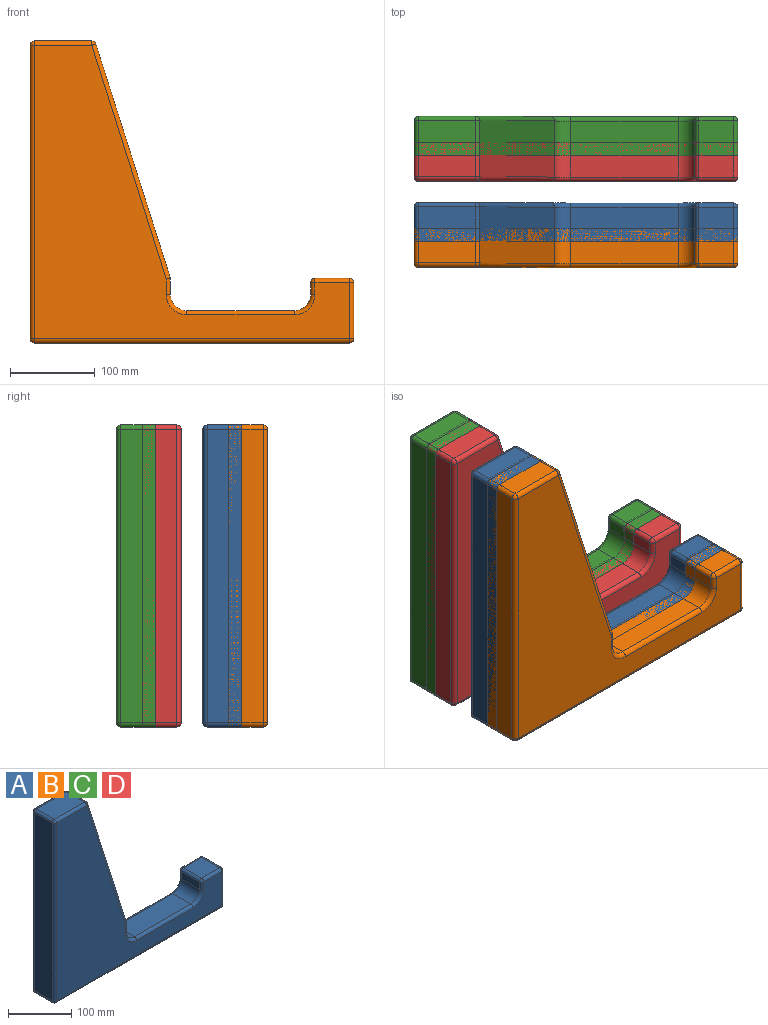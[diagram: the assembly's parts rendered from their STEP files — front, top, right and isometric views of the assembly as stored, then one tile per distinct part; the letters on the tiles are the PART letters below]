
ASSEMBLY  parts=4 mates=1
PART A: 56 faces, bbox 381x50.8x355.6 mm
  f0: plane 345.44x40.64mm, normal (-1,0,0), area 14038.7mm2, adj f23,f32,f33,f34
  f1: plane 370.84x40.64mm, normal (0,0,-1), area 15070.9mm2, adj f14,f22,f23,f24
  f2: plane 66.04x40.64mm, normal (1,0,0), area 2683.9mm2, adj f13,f14,f15,f16
  f3: plane 40.64x40.64mm, normal (0,0,1), area 1651.6mm2, adj f16,f21,f25,f26
  f4: plane 40.64x13.97mm, normal (-1,0,0), area 567.7mm2, adj f5,f26,f31,f35
  f5: cylinder r=19.05mm len=40.64mm, axis (0,1,0), area 1216.1mm2, adj f4,f6,f36,f39
  f6: plane 127x40.64mm, normal (0,0,1), area 5161.3mm2, adj f5,f7,f40,f44
  f7: cylinder r=19.05mm len=40.64mm, axis (0,1,0), area 1216.1mm2, adj f6,f8,f45,f48
  f8: plane 40.64x18.26mm, normal (1,0,0), area 742.1mm2, adj f7,f49,f52,f55
  f9: plane 275.11x87.53mm, normal (0.95,0,0.3), area 11732.7mm2, adj f42,f50,f51,f55
  f10: plane 67.41x40.64mm, normal (0,0,1), area 2739.4mm2, adj f33,f41,f42,f43
  f11: plane 370.84x345.44mm, normal (0,-1,0), area 49312.2mm2, adj f13,f21,f22,f31,f32,f36,f40,f41
  f12: plane 370.84x345.44mm, normal (0,1,0), area 49312.2mm2, adj f15,f24,f25,f34,f35,f39,f43,f44
  f13: cylinder r=5.08mm len=66.04mm, axis (0,0,-1), area 527mm2, adj f2,f11,f17,f18
  f14: cylinder r=5.08mm len=40.64mm, axis (0,1,0), area 324.3mm2, adj f1,f2,f18,f19
  f15: cylinder r=5.08mm len=66.04mm, axis (0,0,1), area 527mm2, adj f2,f12,f19,f20
  f16: cylinder r=5.08mm len=40.64mm, axis (0,-1,0), area 324.3mm2, adj f2,f3,f17,f20
  f17: sphere r=5.08mm, area 40.5mm2, adj f13,f16,f21
  f18: sphere r=5.08mm, area 40.5mm2, adj f13,f14,f22
  f19: sphere r=5.08mm, area 40.5mm2, adj f14,f15,f24
  f20: sphere r=5.08mm, area 40.5mm2, adj f15,f16,f25
  f21: cylinder r=5.08mm len=40.64mm, axis (1,0,0), area 324.3mm2, adj f3,f11,f17,f27
  f22: cylinder r=5.08mm len=370.84mm, axis (-1,0,0), area 2959.2mm2, adj f1,f11,f18,f28
  f23: cylinder r=5.08mm len=40.64mm, axis (0,-1,0), area 324.3mm2, adj f0,f1,f28,f29
  f24: cylinder r=5.08mm len=370.84mm, axis (1,0,0), area 2959.2mm2, adj f1,f12,f19,f29
  f25: cylinder r=5.08mm len=40.64mm, axis (-1,0,0), area 324.3mm2, adj f3,f12,f20,f30
  f26: cylinder r=5.08mm len=40.64mm, axis (0,-1,0), area 324.3mm2, adj f3,f4,f27,f30
  f27: sphere r=5.08mm, area 40.5mm2, adj f21,f26,f31
  f28: sphere r=5.08mm, area 40.5mm2, adj f22,f23,f32
  f29: sphere r=5.08mm, area 40.5mm2, adj f23,f24,f34
  f30: sphere r=5.08mm, area 40.5mm2, adj f25,f26,f35
  f31: cylinder r=5.08mm len=13.97mm, axis (0,0,1), area 111.5mm2, adj f4,f11,f27,f36
  f32: cylinder r=5.08mm len=345.44mm, axis (0,0,1), area 2756.5mm2, adj f0,f11,f28,f37
  f33: cylinder r=5.08mm len=40.64mm, axis (0,1,0), area 324.3mm2, adj f0,f10,f37,f38
  f34: cylinder r=5.08mm len=345.44mm, axis (0,0,-1), area 2756.5mm2, adj f0,f12,f29,f38
  f35: cylinder r=5.08mm len=13.97mm, axis (0,0,-1), area 111.5mm2, adj f4,f12,f30,f39
  f36: torus R=24.13mm, axis (0,-1,0), area 261.9mm2, adj f5,f11,f31,f40
  f37: sphere r=5.08mm, area 40.5mm2, adj f32,f33,f41
  f38: sphere r=5.08mm, area 40.5mm2, adj f33,f34,f43
  f39: torus R=24.13mm, axis (0,-1,0), area 261.9mm2, adj f5,f12,f35,f44
  f40: cylinder r=5.08mm len=127mm, axis (1,0,0), area 1013.4mm2, adj f6,f11,f36,f45
  f41: cylinder r=5.08mm len=67.41mm, axis (1,0,0), area 537.9mm2, adj f10,f11,f37,f46
  f42: cylinder r=5.08mm len=40.64mm, axis (0,1,0), area 260.7mm2, adj f9,f10,f46,f47
  f43: cylinder r=5.08mm len=67.41mm, axis (-1,0,0), area 537.9mm2, adj f10,f12,f38,f47
  f44: cylinder r=5.08mm len=127mm, axis (-1,0,0), area 1013.4mm2, adj f6,f12,f39,f48
  f45: torus R=24.13mm, axis (0,-1,0), area 261.9mm2, adj f7,f11,f40,f49
  f46: sphere r=5.08mm, area 32.6mm2, adj f41,f42,f50
  f47: sphere r=5.08mm, area 32.6mm2, adj f42,f43,f51
  f48: torus R=24.13mm, axis (0,-1,0), area 261.9mm2, adj f7,f12,f44,f52
  f49: cylinder r=5.08mm len=18.26mm, axis (0,0,-1), area 145.7mm2, adj f8,f11,f45,f53
  f50: cylinder r=5.08mm len=276.65mm, axis (0.3,0,-0.95), area 2303.7mm2, adj f9,f11,f46,f53
  f51: cylinder r=5.08mm len=276.65mm, axis (-0.3,0,0.95), area 2303.7mm2, adj f9,f12,f47,f54
  f52: cylinder r=5.08mm len=18.26mm, axis (0,0,1), area 145.7mm2, adj f8,f12,f48,f54
  f53: sphere r=5.08mm, area 7.9mm2, adj f49,f50,f55
  f54: sphere r=5.08mm, area 7.9mm2, adj f51,f52,f55
  f55: cylinder r=5.08mm len=40.64mm, axis (0,1,0), area 63.6mm2, adj f8,f9,f53,f54
PART B: same geometry as A
PART C: same geometry as A
PART D: same geometry as A
PLACE A t=(72.56,-198.13,5.99)mm
PLACE B t=(72.56,-223.53,5.99)mm
PLACE C t=(72.56,-96.53,5.99)mm
PLACE D t=(72.56,-121.93,5.99)mm
MATE parallel D.f12 <-> B.f12  axis (0,1,0) through (-15.09,-121.93,101.83)mm
